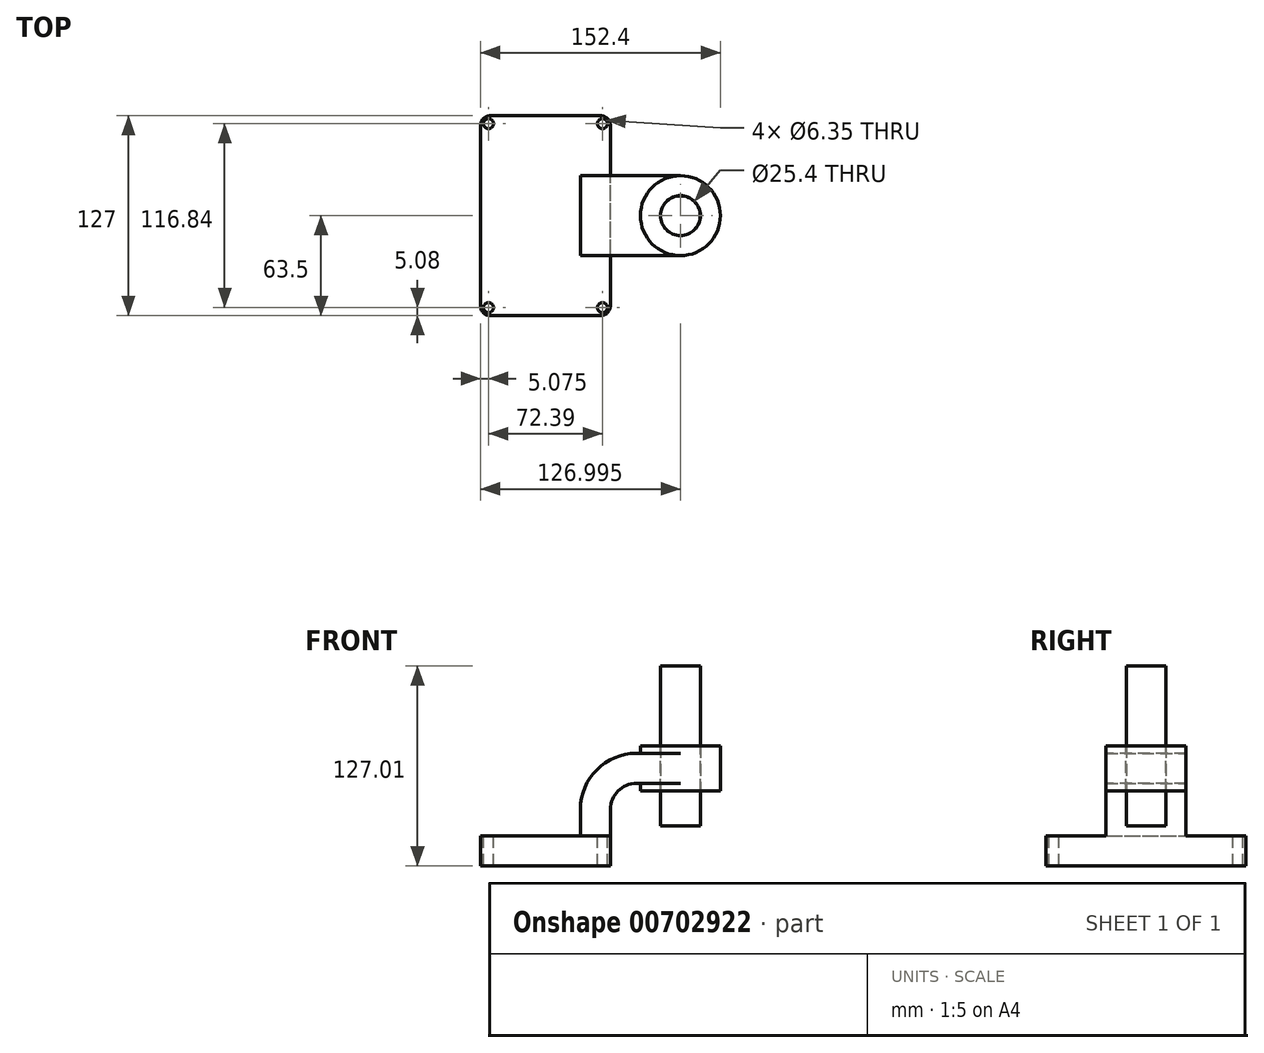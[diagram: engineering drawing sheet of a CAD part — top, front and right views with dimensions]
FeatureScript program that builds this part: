
annotation { "Feature Type Name" : "Feature", "Feature Type Description" : "" }
export const myFeature = defineFeature(function(context is Context, id is Id, definition is map)
    precondition{}
    {
        {
            var Q0;
            Q0=qCreatedBy(makeId("Front.planeOp"),FACE);
            var sketch = newSketch(context, id + "F0", { "sketchPlane" : qUnion([Q0])});
            skLineSegment(sketch, "E0.bottom", {"start": v(41.27, 9.53) * mm, "end": v(-41.28, 9.53) * mm});
            skLineSegment(sketch, "E0.top", {"start": v(41.28, -9.52) * mm, "end": v(-41.27, -9.52) * mm});
            skLineSegment(sketch, "E0.left", {"start": v(41.28, 9.53) * mm, "end": v(41.28, -9.52) * mm});
            skLineSegment(sketch, "E0.right", {"start": v(-41.28, 9.53) * mm, "end": v(-41.27, -9.52) * mm});
            skPoint(sketch, "E0.middle", {"position": v(0, 0) * mm});
            skLineSegment(sketch, "E1.bottom", {"start": v(111.12, 38.1) * mm, "end": v(60.32, 38.1) * mm});
            skLineSegment(sketch, "E1.top", {"start": v(111.12, 66.68) * mm, "end": v(60.32, 66.68) * mm});
            skLineSegment(sketch, "E1.left", {"start": v(111.12, 38.1) * mm, "end": v(111.12, 66.68) * mm});
            skLineSegment(sketch, "E1.right", {"start": v(60.32, 38.1) * mm, "end": v(60.32, 66.68) * mm});
            skPoint(sketch, "E1.middle", {"position": v(85.72, 52.39) * mm});
            skLineSegment(sketch, "E2", {"start": v(41.27, 9.53) * mm, "end": v(41.27, 26.37) * mm});
            skArc(sketch, "E3", {"start": v(41.27, 26.37) * mm, "mid": v(46.11, 38.04) * mm, "end": v(57.79, 42.88) * mm});
            skLineSegment(sketch, "E4", {"start": v(57.79, 42.88) * mm, "end": v(85.72, 42.88) * mm});
            skLineSegment(sketch, "E5.0", {"start": v(57.79, 61.93) * mm, "end": v(85.73, 61.93) * mm});
            skArc(sketch, "E5.1", {"start": v(22.22, 26.37) * mm, "mid": v(32.64, 51.5) * mm, "end": v(57.79, 61.93) * mm});
            skLineSegment(sketch, "E5.2", {"start": v(22.22, 9.53) * mm, "end": v(22.22, 26.37) * mm});
            skLineSegment(sketch, "E6", {"start": v(85.73, 66.68) * mm, "end": v(85.73, 38.1) * mm});
            skFitSpline(sketch, "E7", {"points": [v(-41.28, 9.53) * mm, v(57.79, 61.93) * mm], "startDerivative": vector(45.83, 80.25) * mm, "endDerivative": vector(138.73, -6.77) * mm});
            skSolve(sketch);
        }
        {
            var Q0;
            Q0=makeQuery(id+"F0.imprint","IMPRINT",FACE,{"disambiguationData":[TD([[makeQuery(id+"F0.imprint","IMPRINT",EDGE,{"derivedFrom":sQuery(id+"F0.wireOp",EDGE,"E0.top")}),-1.0]])]});
            extrude(context, id + "F1", {"entities" : qUnion([Q0]), "endBound" : BoundingType.SYMMETRIC, "depth" : 127 * mm, "offsetDistance" : 25.4 * mm});
        }
        {
            var Q0;
            {var subQ1=sQuery(id+"F0.wireOp",EDGE,"E2");Q0=makeQuery(id+"F0.imprint","IMPRINT",FACE,{"disambiguationData":[TD([[makeQuery(id+"F0.imprint","IMPRINT",EDGE,{"derivedFrom":subQ1}),1.0]])]});}
            var Q1;
            {var subQ0=sQuery(id+"F0.wireOp",EDGE,"E4");var subQ1=sQuery(id+"F0.wireOp",EDGE,"E1.right");var subQ2=makeQuery(id+"F0.imprint","INTERSECT",VERTEX,{"derivedFrom":[subQ1,subQ0]});Q1=makeQuery(id+"F0.imprint","IMPRINT",FACE,{"disambiguationData":[TD([[makeQuery(id+"F0.imprint","IMPRINT",EDGE,{"disambiguationData":[TD([[subQ2,-1.0]])],"derivedFrom":subQ1}),-1.0]])]});}
            extrude(context, id + "F2", {"entities" : qUnion([Q0, Q1]), "operationType" : NewBodyOperationType.ADD, "endBound" : BoundingType.SYMMETRIC, "depth" : 50.8 * mm, "offsetDistance" : 25.4 * mm});
        }
        {
            var Q0;
            Q0=makeQuery(id+"F0.imprint","IMPRINT",FACE,{"disambiguationData":[TD([[makeQuery(id+"F0.imprint","IMPRINT",EDGE,{"derivedFrom":sQuery(id+"F0.wireOp",EDGE,"E5.1")}),1.0]])]});
            extrude(context, id + "F3", {"entities" : qUnion([Q0]), "operationType" : NewBodyOperationType.ADD, "endBound" : BoundingType.SYMMETRIC, "depth" : 15.88 * mm, "offsetDistance" : 25.4 * mm});
        }
        {
            var Q0;
            {var subQ4=sQuery(id+"F0.wireOp",EDGE,"E1.left");Q0=makeQuery(id+"F0.imprint","IMPRINT",FACE,{"disambiguationData":[TD([[makeQuery(id+"F0.imprint","IMPRINT",EDGE,{"derivedFrom":subQ4}),1.0]])]});}
            var Q1;
            Q1=sQuery(id+"F0.wireOp",EDGE,"E6");
            revolve(context, id + "F4", {"operationType" : NewBodyOperationType.ADD, "surfaceOperationType" : NewSurfaceOperationType.NEW, "entities" : qUnion([Q0]), "axis" : qUnion([Q1]), "revolveType" : RevolveType.FULL});
        }
        {
            var Q0;
            Q0=makeQuery(id+"F1.opExtrude","CAP_EDGE",EDGE,{"disambiguationData":[OSD([sQuery(id+"F0.wireOp",EDGE,"E0.right")])],"isStart":false});
            var Q1;
            Q1=makeQuery(id+"F1.opExtrude","CAP_EDGE",EDGE,{"disambiguationData":[OSD([sQuery(id+"F0.wireOp",EDGE,"E0.left")])],"isStart":false});
            var Q2;
            Q2=makeQuery(id+"F1.opExtrude","CAP_EDGE",EDGE,{"disambiguationData":[OSD([sQuery(id+"F0.wireOp",EDGE,"E0.left")])],"isStart":true});
            var Q3;
            Q3=makeQuery(id+"F1.opExtrude","CAP_EDGE",EDGE,{"disambiguationData":[OSD([sQuery(id+"F0.wireOp",EDGE,"E0.right")])],"isStart":true});
            fillet(context, id + "F5", {"entities" : qUnion([Q0, Q1, Q2, Q3]), "radius" : 6.35 * mm, "tangentPropagation" : true, "allowEdgeOverflow" : false});
        }
        {
            var Q0;
            Q0=makeQuery(id+"F4.opRevolve","SWEPT_FACE",FACE,{"disambiguationData":[OSD([sQuery(id+"F0.wireOp",EDGE,"E1.top")])]});
            var sketch = newSketch(context, id + "F6", { "sketchPlane" : qUnion([Q0])});
            skCircle(sketch, "E8", {"center": v(85.72, 0) * mm, "radius": 12.7 * mm});
            skSolve(sketch);
        }
        {
            var Q0;
            Q0=makeQuery(id+"F6.imprint","IMPRINT",FACE,{"disambiguationData":[TD([[makeQuery(id+"F6.imprint","IMPRINT",EDGE,{"derivedFrom":sQuery(id+"F6.wireOp",EDGE,"E8")}),1.0]])]});
            extrude(context, id + "F7", {"entities" : qUnion([Q0]), "operationType" : NewBodyOperationType.REMOVE, "oppositeDirection" : true, "depth" : 30.48 * mm, "offsetDistance" : 25.4 * mm});
        }
        {
            var Q0;
            {var subQ3=sQuery(id+"F0.wireOp",EDGE,"E0.bottom");var subQ5=sQuery(id+"F0.wireOp",EDGE,"E0.right");var subQ6=sQuery(id+"F0.wireOp",EDGE,"E0.left");Q0=makeQuery(id+"F3.boolean.opBoolean","SPLIT",FACE,{"disambiguationData":[TD([makeQuery(id+"F1.opExtrude","CAP_FACE",FACE,{"disambiguationData":[OSD([subQ3,sQuery(id+"F0.wireOp",EDGE,"E0.top"),subQ6,subQ5])],"isStart":false})])],"derivedFrom":makeQuery(id+"F1.opExtrude","SWEPT_FACE",FACE,{"disambiguationData":[OSD([subQ3])]})});}
            var sketch = newSketch(context, id + "F8", { "sketchPlane" : qUnion([Q0])});
            skCircle(sketch, "E9", {"center": v(-36.2, 58.42) * mm, "radius": 3.18 * mm});
            skCircle(sketch, "E10", {"center": v(36.2, 58.42) * mm, "radius": 3.18 * mm});
            skCircle(sketch, "E11", {"center": v(36.2, -58.42) * mm, "radius": 3.18 * mm});
            skCircle(sketch, "E12", {"center": v(-36.2, -58.42) * mm, "radius": 3.18 * mm});
            skSolve(sketch);
        }
        {
            var Q0;
            Q0=makeQuery(id+"F8.imprint","IMPRINT",FACE,{"disambiguationData":[TD([[makeQuery(id+"F8.imprint","IMPRINT",EDGE,{"derivedFrom":sQuery(id+"F8.wireOp",EDGE,"E9")}),1.0]])]});
            var Q1;
            Q1=makeQuery(id+"F8.imprint","IMPRINT",FACE,{"disambiguationData":[TD([[makeQuery(id+"F8.imprint","IMPRINT",EDGE,{"derivedFrom":sQuery(id+"F8.wireOp",EDGE,"E10")}),1.0]])]});
            var Q2;
            Q2=makeQuery(id+"F8.imprint","IMPRINT",FACE,{"disambiguationData":[TD([[makeQuery(id+"F8.imprint","IMPRINT",EDGE,{"derivedFrom":sQuery(id+"F8.wireOp",EDGE,"E11")}),1.0]])]});
            var Q3;
            Q3=makeQuery(id+"F8.imprint","IMPRINT",FACE,{"disambiguationData":[TD([[makeQuery(id+"F8.imprint","IMPRINT",EDGE,{"derivedFrom":sQuery(id+"F8.wireOp",EDGE,"E12")}),1.0]])]});
            extrude(context, id + "F9", {"entities" : qUnion([Q0, Q1, Q2, Q3]), "operationType" : NewBodyOperationType.REMOVE, "oppositeDirection" : true, "depth" : 25.4 * mm, "offsetDistance" : 25.4 * mm});
        }
        {
            var Q0;
            Q0=makeQuery(id+"F4.opRevolve","SWEPT_FACE",FACE,{"disambiguationData":[OSD([sQuery(id+"F0.wireOp",EDGE,"E1.top")])]});
            var sketch = newSketch(context, id + "F10", { "sketchPlane" : qUnion([Q0])});
            skCircle(sketch, "E13", {"center": v(85.72, 0) * mm, "radius": 12.57 * mm});
            skSolve(sketch);
        }
        {
            var Q0;
            Q0=makeQuery(id+"F10.imprint","IMPRINT",FACE,{"disambiguationData":[TD([[makeQuery(id+"F10.imprint","IMPRINT",EDGE,{"derivedFrom":sQuery(id+"F10.wireOp",EDGE,"E13")}),1.0]])]});
            extrude(context, id + "F11", {"entities" : qUnion([Q0]), "endBound" : BoundingType.SYMMETRIC, "depth" : 101.6 * mm, "offsetDistance" : 25.4 * mm});
        }
    });
